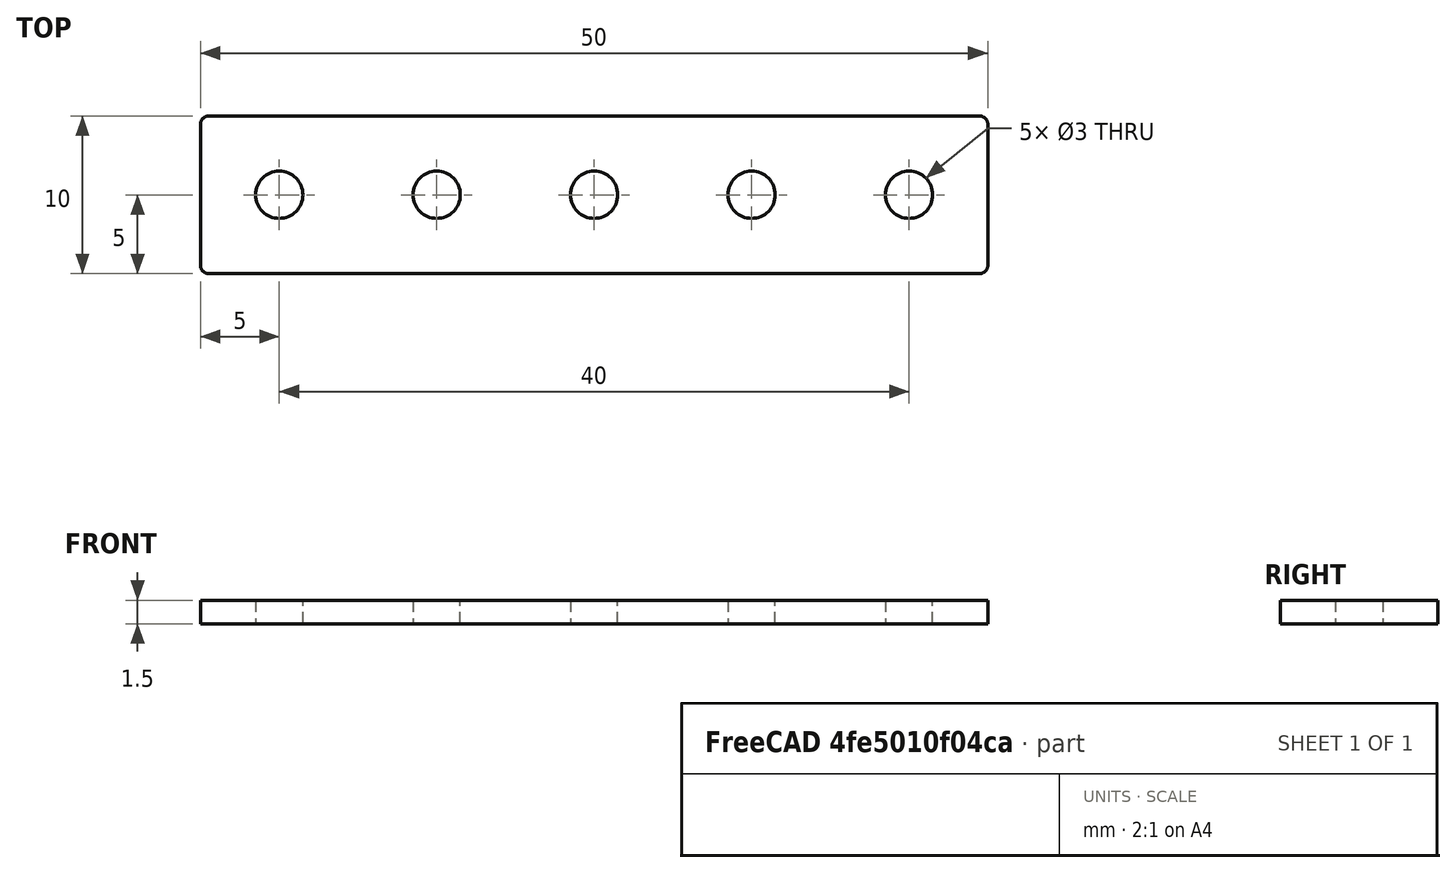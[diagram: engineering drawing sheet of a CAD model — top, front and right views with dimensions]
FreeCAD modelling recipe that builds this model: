
FCSTD DOCUMENT  (FreeCAD 0.18R16146 (Git))
Label: makerbeam_bracket_straight
License: All rights reserved
LicenseURL: http://en.wikipedia.org/wiki/All_rights_reserved
objects: Sketcher::SketchObject×1, PartDesign::Pad×1, PartDesign::Fillet×1, PartDesign::Body×1
note: 5 computed .brp shape members not serialized (recipe doc carries the construction recipe); baked Part::Feature solids carry a one-line shape summary decoded from their .brp

FEATURE [Sketcher::SketchObject] Sketch
  MapMode = 5
  Support = -> [XY_Plane]
  sketch-geometry (9):
    g0: Circle CenterX=-20 CenterY=0 CenterZ=0 NormalX=0 NormalY=0 NormalZ=1 AngleXU=0 Radius=1.5
    g1: Circle CenterX=-10 CenterY=0 CenterZ=0 NormalX=0 NormalY=0 NormalZ=1 AngleXU=0 Radius=1.5
    g2: Circle CenterX=0 CenterY=0 CenterZ=0 NormalX=0 NormalY=0 NormalZ=1 AngleXU=0 Radius=1.5
    g3: Circle CenterX=10 CenterY=0 CenterZ=0 NormalX=0 NormalY=0 NormalZ=1 AngleXU=0 Radius=1.5
    g4: Circle CenterX=20 CenterY=0 CenterZ=0 NormalX=0 NormalY=0 NormalZ=1 AngleXU=0 Radius=1.5
    g5: LineSegment StartX=-25 StartY=5 StartZ=0 EndX=25 EndY=5 EndZ=0
    g6: LineSegment StartX=25 StartY=5 StartZ=0 EndX=25 EndY=-5 EndZ=0
    g7: LineSegment StartX=25 StartY=-5 StartZ=0 EndX=-25 EndY=-5 EndZ=0
    g8: LineSegment StartX=-25 StartY=-5 StartZ=0 EndX=-25 EndY=5 EndZ=0
  constraints (15):
    c: Radius(g0) = 1.5
    c: Equal(g0,g1) = 1.5
    c: Equal(g0,g2) = 1.5
    c: Equal(g0,g3) = 1.5
    c: Equal(g0,g4) = 1.5
    c: Coincident(g5,g6)
    c: Coincident(g6,g7)
    c: Coincident(g7,g8)
    c: Coincident(g8,g5)
    c: Horizontal(g5)
    c: Horizontal(g7)
    c: Vertical(g6)
    c: Vertical(g8)
    c: DistanceX(g7,g7) = 50
    c: DistanceY(g6,g6) = 10
FEATURE [PartDesign::Pad] Pad
  Length = 1.5
  Length2 = 100
  Profile = -> Sketch
  Type = 0
FEATURE [PartDesign::Fillet] Fillet
  Base = -> Pad [Edge2,Edge5,Edge8,Edge1]
  BaseFeature = -> Pad
  Radius = 0.5
FEATURE [PartDesign::Body] Body  label="makerbeam_bracket_straight"
  Group = -> [Sketch,Pad,Fillet]
  Origin = -> Origin
  Tip = -> Fillet
